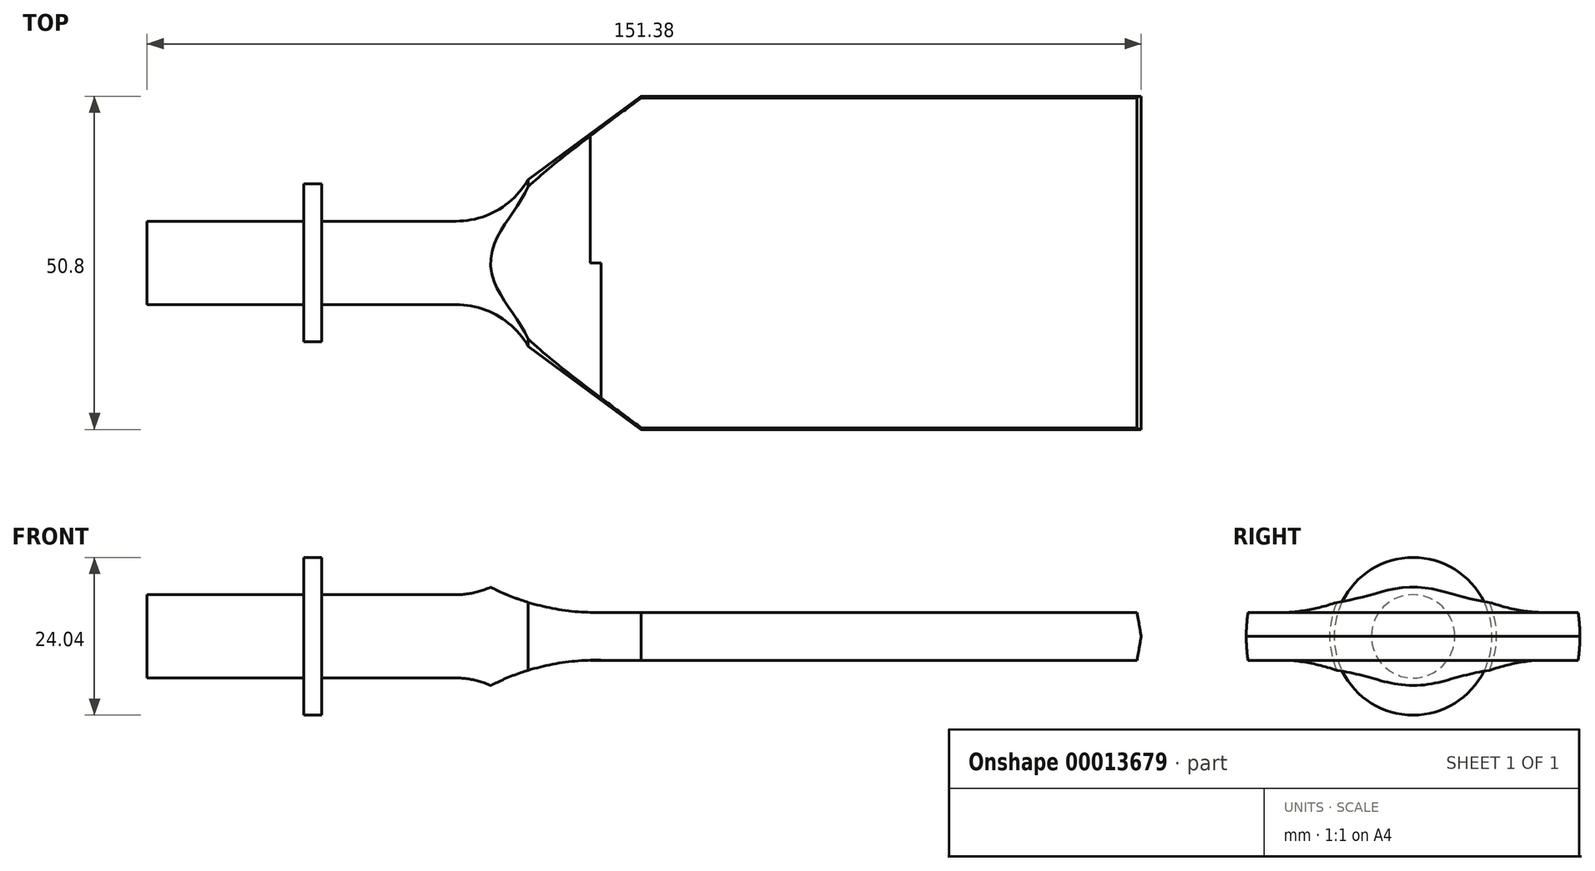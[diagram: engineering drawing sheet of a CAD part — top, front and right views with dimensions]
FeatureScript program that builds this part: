
annotation { "Feature Type Name" : "Feature", "Feature Type Description" : "" }
export const myFeature = defineFeature(function(context is Context, id is Id, definition is map)
    precondition{}
    {
        {
            var Q0;
            Q0=qCreatedBy(makeId("Front.planeOp"),FACE);
            var sketch = newSketch(context, id + "F0", { "sketchPlane" : qUnion([Q0])});
            skLineSegment(sketch, "E0", {"start": v(0, 0) * mm, "end": v(0, 6.35) * mm});
            skLineSegment(sketch, "E1", {"start": v(0, 6.35) * mm, "end": v(23.84, 6.35) * mm});
            skLineSegment(sketch, "E2", {"start": v(23.84, 6.35) * mm, "end": v(23.84, 12.02) * mm});
            skLineSegment(sketch, "E3", {"start": v(23.84, 12.02) * mm, "end": v(26.57, 12.02) * mm});
            skLineSegment(sketch, "E4", {"start": v(26.57, 12.02) * mm, "end": v(26.57, 6.35) * mm});
            skLineSegment(sketch, "E5", {"start": v(26.57, 6.35) * mm, "end": v(47.04, 6.35) * mm});
            skLineSegment(sketch, "E6", {"start": v(75.22, 25.4) * mm, "end": v(75.22, 0) * mm});
            skLineSegment(sketch, "E7", {"start": v(75.22, 0) * mm, "end": v(0, 0) * mm});
            skPoint(sketch, "E8.visualSharp", {"position": v(59.74, 6.35) * mm});
            skArc(sketch, "E8.filletArc", {"start": v(47.04, 6.35) * mm, "mid": v(53.4, 8.05) * mm, "end": v(58.04, 12.7) * mm});
            skLineSegment(sketch, "E9", {"start": v(58.04, 12.7) * mm, "end": v(75.22, 25.4) * mm});
            skSolve(sketch);
        }
        {
            var Q0;
            Q0=makeQuery(id+"F0.imprint","IMPRINT",FACE,{"disambiguationData":[TD([[makeQuery(id+"F0.imprint","IMPRINT",EDGE,{"derivedFrom":sQuery(id+"F0.wireOp",EDGE,"E0")}),-1.0]])]});
            var Q1;
            Q1=sQuery(id+"F0.wireOp",EDGE,"E7");
            revolve(context, id + "F1", {"entities" : qUnion([Q0]), "axis" : qUnion([Q1]), "revolveType" : RevolveType.FULL});
        }
        {
            var Q0;
            Q0=qCreatedBy(makeId("Front.planeOp"),FACE);
            var sketch = newSketch(context, id + "F2", { "sketchPlane" : qUnion([Q0])});
            skArc(sketch, "E10", {"start": v(103.16, 42.44) * mm, "mid": v(41.97, 61.8) * mm, "end": v(69.12, 3.65) * mm});
            skLineSegment(sketch, "E11", {"start": v(67.5, 3.65) * mm, "end": v(134.04, 3.65) * mm});
            skLineSegment(sketch, "E12", {"start": v(134.04, 3.65) * mm, "end": v(103.16, 42.44) * mm});
            skLineSegment(sketch, "E13", {"start": v(0, 0) * mm, "end": v(-15.75, 0) * mm});
            skLineSegment(sketch, "E14.MirrorCS", {"start": v(67.5, -3.65) * mm, "end": v(134.04, -3.65) * mm});
            skArc(sketch, "E15.MirrorCS", {"start": v(103.16, -42.44) * mm, "mid": v(41.97, -61.8) * mm, "end": v(69.12, -3.65) * mm});
            skLineSegment(sketch, "E16.MirrorCS", {"start": v(134.04, -3.65) * mm, "end": v(103.16, -42.44) * mm});
            skSolve(sketch);
        }
        {
            var Q0;
            {var subQ0=sQuery(id+"F2.wireOp",EDGE,"E12");Q0=makeQuery(id+"F2.imprint","IMPRINT",FACE,{"disambiguationData":[TD([[makeQuery(id+"F2.imprint","IMPRINT",EDGE,{"derivedFrom":subQ0}),1.0]])]});}
            var Q1;
            {var subQ0=sQuery(id+"F2.wireOp",EDGE,"E16.MirrorCS");Q1=makeQuery(id+"F2.imprint","IMPRINT",FACE,{"disambiguationData":[TD([[makeQuery(id+"F2.imprint","IMPRINT",EDGE,{"derivedFrom":subQ0}),-1.0]])]});}
            extrude(context, id + "F3", {"entities" : qUnion([Q0, Q1]), "operationType" : NewBodyOperationType.REMOVE, "oppositeDirection" : true, "depth" : 25.4 * mm});
        }
        {
            var Q0;
            Q0=qSketchRegion(id+"F2",true);
            extrude(context, id + "F4", {"entities" : qUnion([Q0]), "operationType" : NewBodyOperationType.REMOVE, "depth" : 25.4 * mm});
        }
        {
            var Q0;
            Q0=makeQuery(id+"F1.opRevolve","SWEPT_FACE",FACE,{"disambiguationData":[OSD([sQuery(id+"F0.wireOp",EDGE,"E6")])]});
            extrude(context, id + "F5", {"entities" : qUnion([Q0]), "operationType" : NewBodyOperationType.ADD, "depth" : 76.2 * mm});
        }
        {
            var Q0;
            Q0=qCreatedBy(makeId("Front.planeOp"),FACE);
            var sketch = newSketch(context, id + "F6", { "sketchPlane" : qUnion([Q0])});
            skLineSegment(sketch, "E17", {"start": v(0, 0) * mm, "end": v(151.7, 0) * mm});
            skLineSegment(sketch, "E18", {"start": v(151.7, 0) * mm, "end": v(151.38, 0) * mm});
            skLineSegment(sketch, "E19", {"start": v(151.38, 0) * mm, "end": v(150.03, 7.64) * mm});
            skLineSegment(sketch, "E20.MirrorCS", {"start": v(151.38, 0) * mm, "end": v(150.03, -7.64) * mm});
            skLineSegment(sketch, "E21", {"start": v(151.38, 5.57) * mm, "end": v(150.4, 5.57) * mm});
            skLineSegment(sketch, "E22", {"start": v(152.59, -4.6) * mm, "end": v(150.47, -5.16) * mm});
            skLineSegment(sketch, "E23", {"start": v(152.59, -4.6) * mm, "end": v(151.38, 5.57) * mm});
            skSolve(sketch);
        }
        {
            var Q0;
            {var subQ1=sQuery(id+"F6.wireOp",EDGE,"E21");Q0=makeQuery(id+"F6.imprint","IMPRINT",FACE,{"disambiguationData":[TD([[makeQuery(id+"F6.imprint","IMPRINT",EDGE,{"derivedFrom":subQ1}),1.0]])]});}
            extrude(context, id + "F7", {"entities" : qUnion([Q0]), "operationType" : NewBodyOperationType.REMOVE, "oppositeDirection" : true, "depth" : 25.4 * mm});
        }
        {
            var Q0;
            Q0=qSketchRegion(id+"F6",true);
            extrude(context, id + "F8", {"entities" : qUnion([Q0]), "operationType" : NewBodyOperationType.REMOVE, "depth" : 25.4 * mm});
        }
    });
